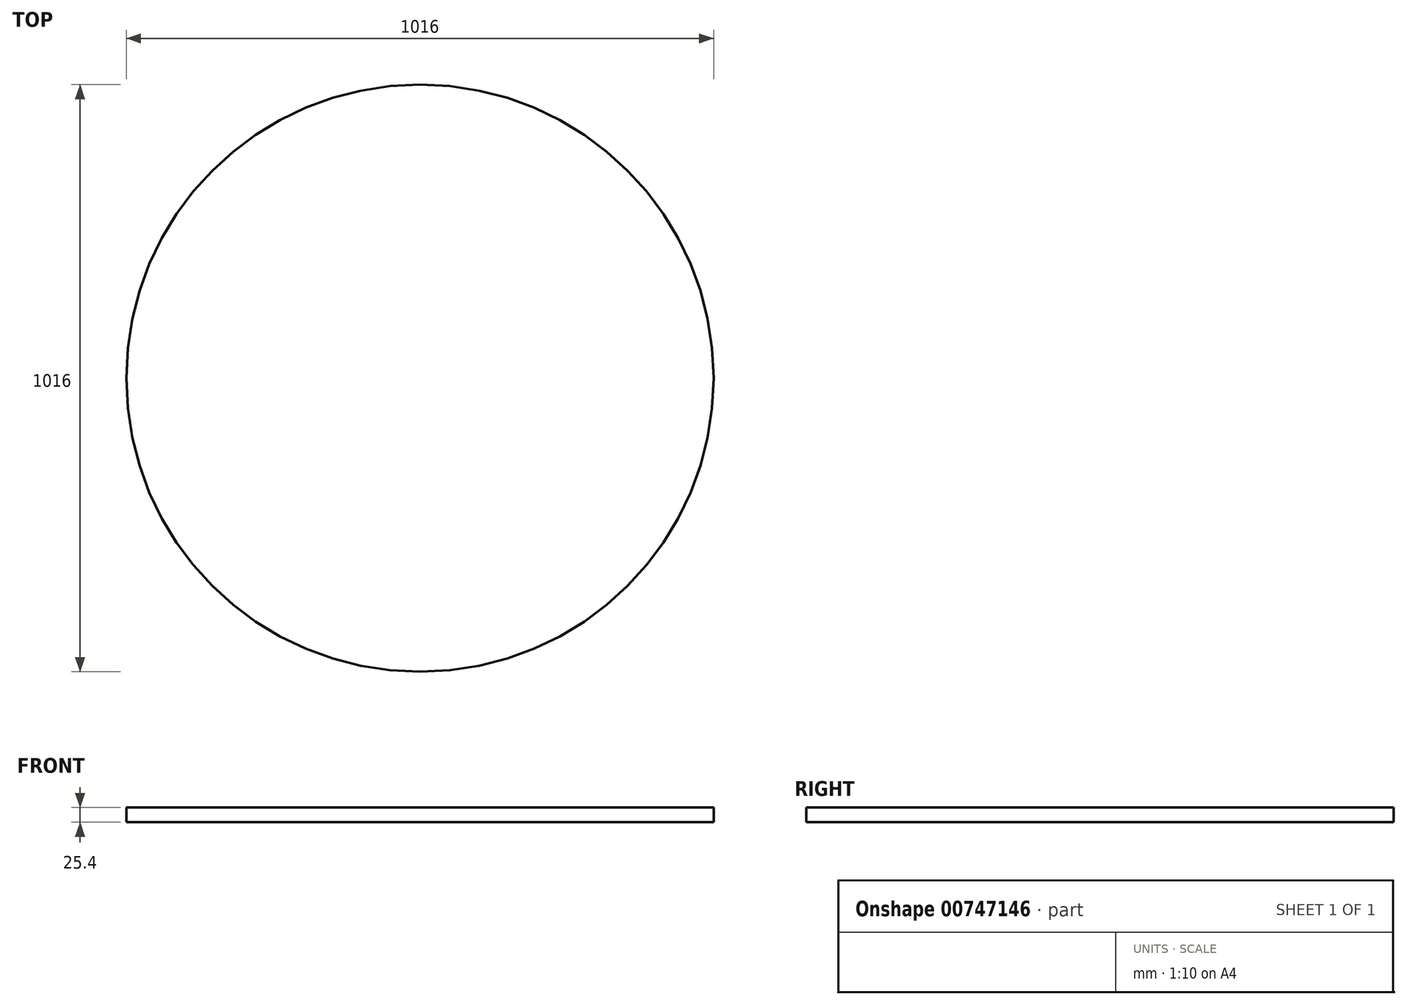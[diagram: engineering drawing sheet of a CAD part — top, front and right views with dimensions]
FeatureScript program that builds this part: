
annotation { "Feature Type Name" : "Feature", "Feature Type Description" : "" }
export const myFeature = defineFeature(function(context is Context, id is Id, definition is map)
    precondition{}
    {
        {
            var Q0;
            Q0=qCreatedBy(makeId("Top.planeOp"),FACE);
            var sketch = newSketch(context, id + "F0", { "sketchPlane" : qUnion([Q0])});
            skCircle(sketch, "E0", {"center": v(0, 0) * mm, "radius": 508 * mm});
            skSolve(sketch);
        }
        {
            var Q0;
            Q0 = qSketchRegion(id + "F0", true);
            extrude(context, id + "F1", {"entities" : qUnion([Q0]), "depth" : 25.4 * mm, "offsetDistance" : 25.4 * mm});
        }
    });
